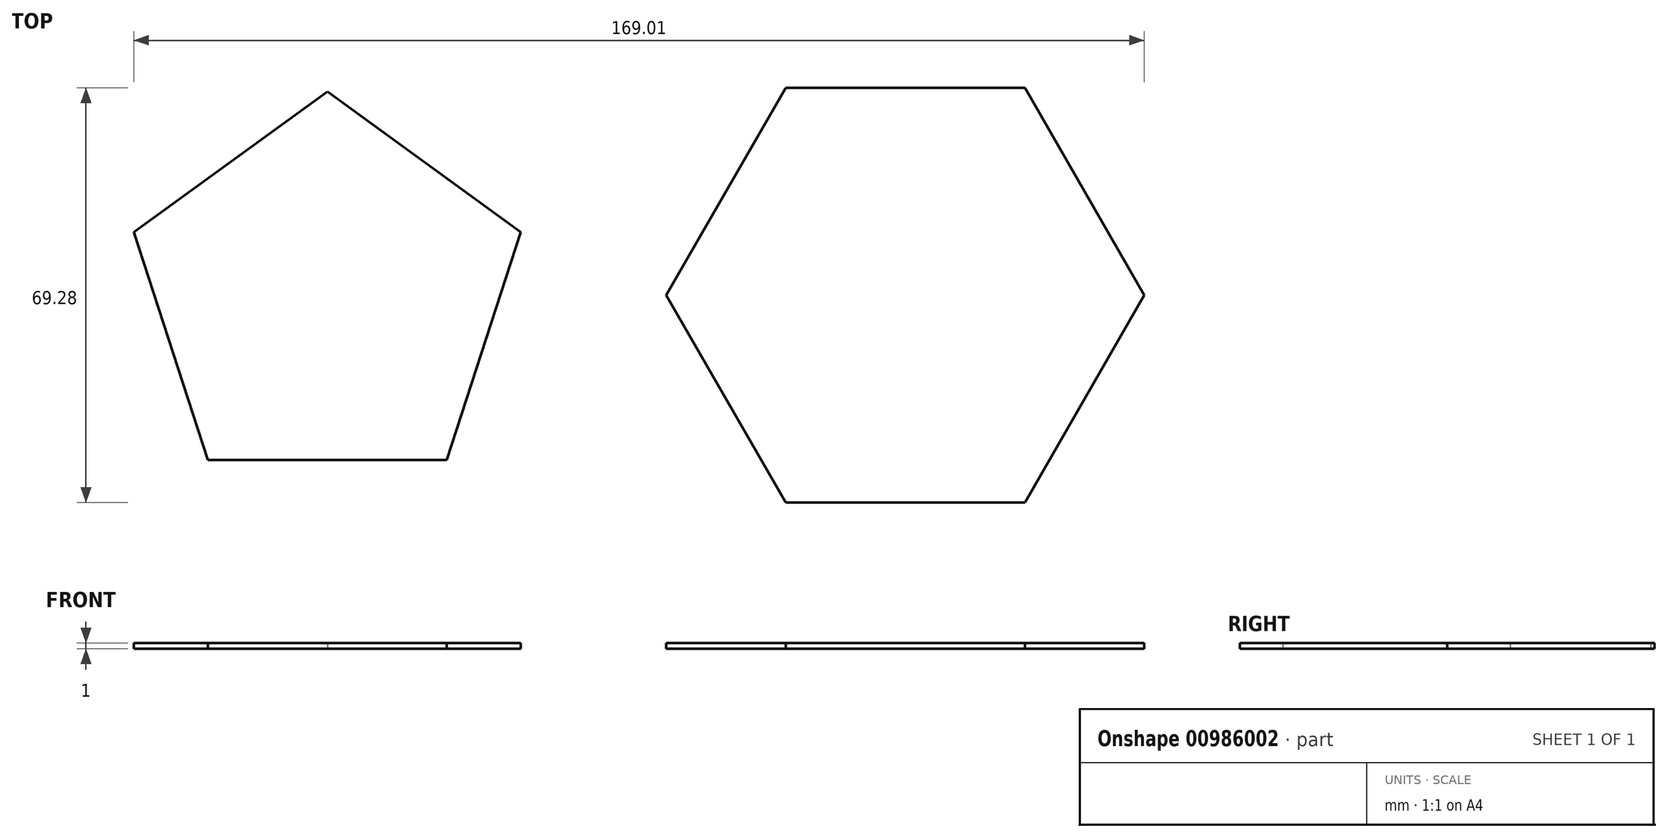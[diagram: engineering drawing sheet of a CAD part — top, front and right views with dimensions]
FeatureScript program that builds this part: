
annotation { "Feature Type Name" : "Feature", "Feature Type Description" : "" }
export const myFeature = defineFeature(function(context is Context, id is Id, definition is map)
    precondition{}
    {
        {
            var Q0;
            Q0=qCreatedBy(makeId("Top.planeOp"),FACE);
            var sketch = newSketch(context, id + "F0", { "sketchPlane" : qUnion([Q0])});
            skCircle(sketch, "E0.cCircle", {"center": v(0, 0) * mm, "radius": 34.64 * mm, "construction": true});
            skLineSegment(sketch, "E0.0", {"start": v(20, -34.64) * mm, "end": v(-20, -34.64) * mm});
            skLineSegment(sketch, "E0.1", {"start": v(-20, -34.64) * mm, "end": v(-40, 0) * mm});
            skLineSegment(sketch, "E0.2", {"start": v(-40, 0) * mm, "end": v(-20, 34.64) * mm});
            skLineSegment(sketch, "E0.3", {"start": v(-20, 34.64) * mm, "end": v(20, 34.64) * mm});
            skLineSegment(sketch, "E0.4", {"start": v(20, 34.64) * mm, "end": v(40, 0) * mm});
            skLineSegment(sketch, "E0.5", {"start": v(40, 0) * mm, "end": v(20, -34.64) * mm});
            skPoint(sketch, "E0.0.midPoint", {"position": v(0, -34.64) * mm});
            skSolve(sketch);
        }
        {
            var Q0;
            Q0 = qSketchRegion(id + "F0", true);
            extrude(context, id + "F1", {"entities" : qUnion([Q0]), "surfaceOperationType" : NewSurfaceOperationType.ADD, "depth" : 1 * mm, "offsetDistance" : 25 * mm});
        }
        {
            var Q0;
            Q0=qCreatedBy(makeId("Top.planeOp"),FACE);
            var sketch = newSketch(context, id + "F2", { "sketchPlane" : qUnion([Q0])});
            skCircle(sketch, "E1.cCircle", {"center": v(-96.65, 0) * mm, "radius": 27.53 * mm, "construction": true});
            skLineSegment(sketch, "E1.0", {"start": v(-76.65, -27.53) * mm, "end": v(-116.65, -27.53) * mm});
            skLineSegment(sketch, "E1.1", {"start": v(-116.65, -27.53) * mm, "end": v(-129.01, 10.51) * mm});
            skLineSegment(sketch, "E1.2", {"start": v(-129.01, 10.51) * mm, "end": v(-96.65, 34.03) * mm});
            skLineSegment(sketch, "E1.3", {"start": v(-96.65, 34.03) * mm, "end": v(-64.3, 10.51) * mm});
            skLineSegment(sketch, "E1.4", {"start": v(-64.3, 10.51) * mm, "end": v(-76.65, -27.53) * mm});
            skPoint(sketch, "E1.0.midPoint", {"position": v(-96.65, -27.53) * mm});
            skSolve(sketch);
        }
        {
            var Q0;
            Q0 = qSketchRegion(id + "F2", true);
            extrude(context, id + "F3", {"entities" : qUnion([Q0]), "depth" : 1 * mm, "offsetDistance" : 25 * mm});
        }
    });
